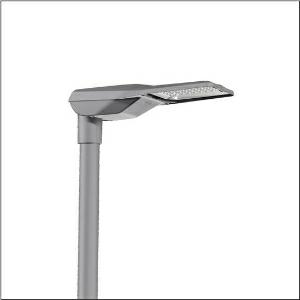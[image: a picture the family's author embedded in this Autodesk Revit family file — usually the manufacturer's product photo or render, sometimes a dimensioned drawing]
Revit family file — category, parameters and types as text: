
# Revit family: streetlight_sl_21_iq_mini___st1_0a_5xe2d21g08hb_8dd2
name_source: partatom
category: Lighting Fixtures
units: mm (PartAtom-declared; Revit-internal decimal feet)

## family parameters
Cut with Voids When Loaded = No
Host = Face
Light Source = No
Part Type = Normal
Room Calculation Point = No
Round Connector Dimension = Use Diameter
Shared = No

## types (1)
- --- (1 x LED, 7830 lm, 70.9 W, 2200K)
    Apparent Load = 71 VA
    CIE Flux Codes = 37 72 97 100 100
    Color Rendering = 70
    Color Temperature = 2200K
    Default Elevation = 1800 mm
    Description = Streetlight SL 21 iQ mini, mast luminaire, primary light control with lens, of PMMA, primary optical cover: cover, of toughened safety glass, transparent, light distribution: ST1.0a, light emission: direct distribution, primary light characteristic: asymmetric, installation type: post-top, side-entry, LED, High Power LED, rated luminous flux: 7.830lm, luminous efficacy: 110lm/W, light colour: 722, colour temperature: 2200K, control gear: iQ Street-Remote, control: Street-Remote, Auto-Match, Temp-Guard, Lumen-Switch, Night-Set, Smart-Wire, Light-Fading, Desk-Remote (wireless, voltage-free reading and setting of iQ features in the workshop via application-optimized NFC function/RFID function), optimised constant luminous flux control (CLO 2.0), pre-setting: linear dimming characteristic, mains connection: 220..240V, AC, 50/60Hz, start of lifetime: 71W, end of service life: 75W, reduction: 31W, luminaire housing, of diecast aluminium, powder-coated, SITECO metallic grey (DB 702S), corrosivity category C5 high according to DIN EN ISO 12944, please order mast flange separately, inclination adjustable: 0°, 5°, 10°, 15°, sealing non-destructively replaceable, multi-level sealing system, length: 628mm, width: 235mm, height: 110mm, mast flange for spigot size: 42mm (side-entry): 5XC10008XM4, 60/48mm (side-entry/post-top): 5XC10108XM2, 76/60mm (side-entry/post-top): 5XC10108XM1, mounting height: 4..8m, protection rating (complete): IP66, insulation class (complete): insulation class II (safety insulation), certification: CE, ENEC, ENEC+, VDE, impact resistance: IK10, permissible operating ambient temperature for outdoor applications: -40..+50°C, standard-compliant lighting for roads and squares, packaging unit: 1 piece

Light Distribution: ST1.0a
    Height = 110 mm
    Lamp = 1 x LED
    Lamp Light Flux = 7830 lm
    Lamp Power = 70.9 W
    Lamp count = 1
    Length = 625 mm
    Luminous efficacy = 110 lm/W
    Manufacturer = Siteco
    ModVariant = No
    Model = 5XE2D21G08HB
    Number of Poles = 1
    OnlyDefault = Yes
    Power Factor = 1
    Product Name = Streetlight SL 21 iQ mini | ST1.0a
    Product group = mast luminaire | pylon top
    ProductGroupID = 6100
    Protection Class = Protection class II
    Protection Degree = IP 66
    RLX_Detail_Level = 1
    RLX_Emergency_Light_Flux = 0 lm
    RLX_Emergency_Type = 0
    RLX_Emergency_Type_DB = No
    RlxData = <blob elided: 26273 chars, md5=5d303c78>
    Socket = socket
    Standby Power = 0 W
    System Light Flux = 7830 lm
    System Power = 71 W
    Type Comments = factory setting: luminous flux: 100 % | dim-lin: 254 | 711 mA
    Type Image = l_1003519.jpg
    URL = http://relux.com
    VarID = @adj_157755
    Voltage = 0 V
    Weight = 0.00 kg
    Width = 234 mm

## geometry (parser evidence)
native form markers: Blend x4, Sweep x10
no freeform markers — native parametric forms only
